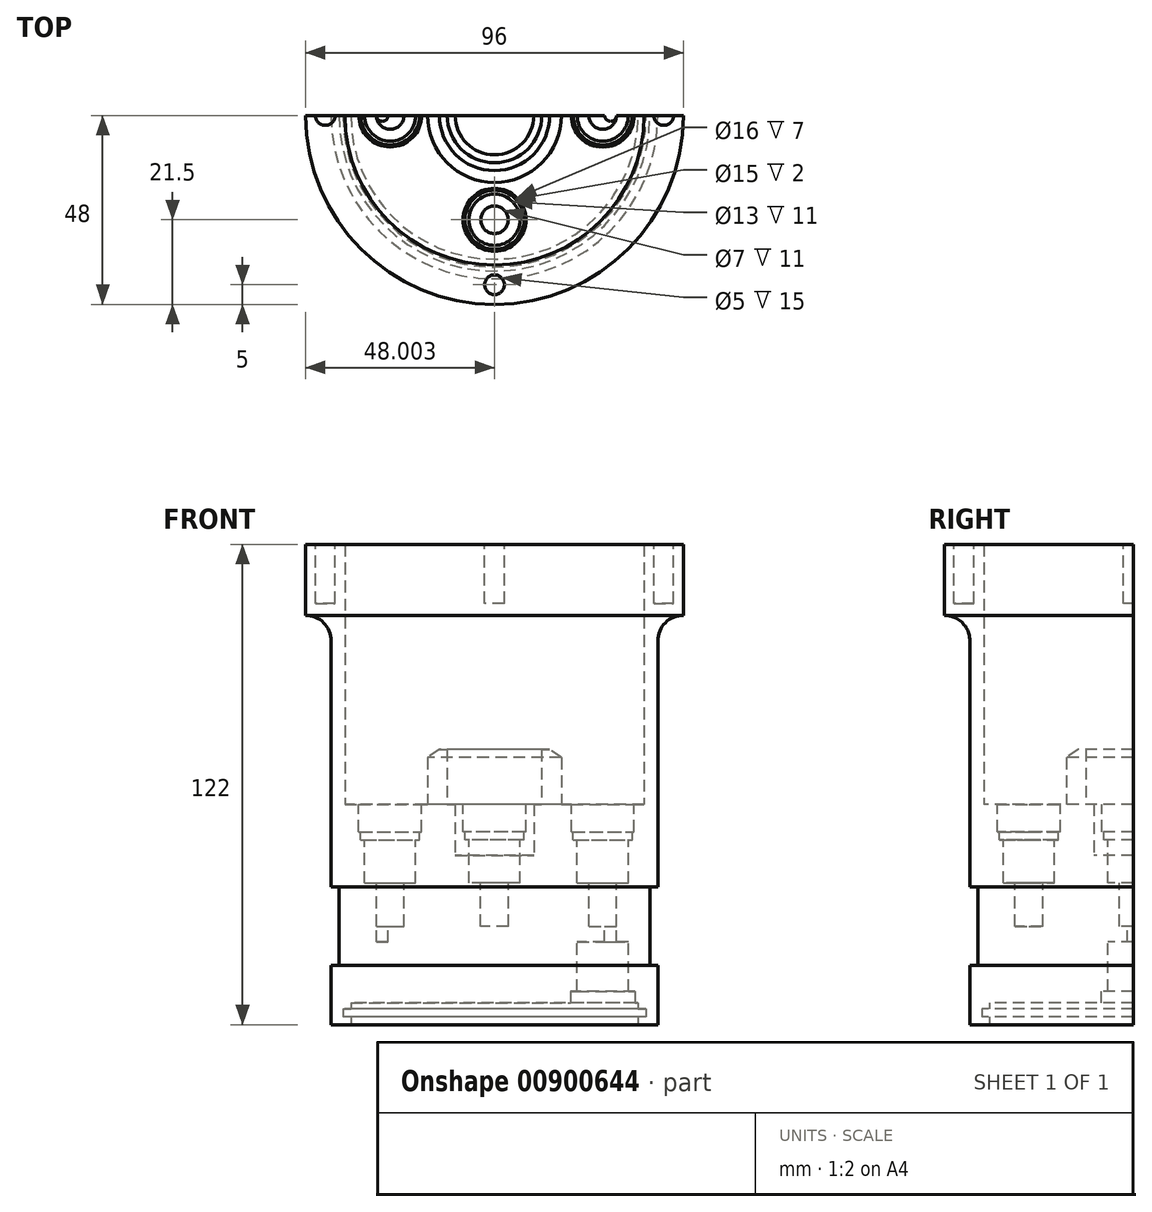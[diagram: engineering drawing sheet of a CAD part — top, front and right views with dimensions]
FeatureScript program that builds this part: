
annotation { "Feature Type Name" : "Feature", "Feature Type Description" : "" }
export const myFeature = defineFeature(function(context is Context, id is Id, definition is map)
    precondition{}
    {
        {
            var Q0;
            Q0=qCreatedBy(makeId("Front.planeOp"),FACE);
            var sketch = newSketch(context, id + "F0", { "sketchPlane" : qUnion([Q0])});
            skLineSegment(sketch, "E0.bottom", {"start": v(54.77, 57.03) * mm, "end": v(58.27, 57.03) * mm});
            skLineSegment(sketch, "E0.top", {"start": v(53.27, -64.97) * mm, "end": v(58.27, -64.97) * mm});
            skLineSegment(sketch, "E0.right", {"start": v(58.27, 32.53) * mm, "end": v(58.27, -29.97) * mm});
            skLineSegment(sketch, "E1", {"start": v(54.77, 57.03) * mm, "end": v(54.77, -8.97) * mm});
            skLineSegment(sketch, "E2", {"start": v(54.77, -8.97) * mm, "end": v(33.77, -8.97) * mm});
            skLineSegment(sketch, "E3.top", {"start": v(30.77, 4.9) * mm, "end": v(28.77, 4.9) * mm});
            skLineSegment(sketch, "E3.left", {"start": v(33.77, -8.97) * mm, "end": v(33.77, 2.9) * mm});
            skLineSegment(sketch, "E3.right", {"start": v(28.77, -8.97) * mm, "end": v(28.77, 4.9) * mm});
            skLineSegment(sketch, "E4", {"start": v(30.77, 4.9) * mm, "end": v(33.77, 2.9) * mm});
            skPoint(sketch, "E5.orphan", {"position": v(33.77, 4.9) * mm});
            skLineSegment(sketch, "E6.trimOffspring", {"start": v(28.77, -8.97) * mm, "end": v(26.77, -8.97) * mm});
            skLineSegment(sketch, "E7.left", {"start": v(26.77, -8.97) * mm, "end": v(26.77, -10.97) * mm});
            skLineSegment(sketch, "E8.top", {"start": v(26.77, -21.97) * mm, "end": v(16.77, -21.97) * mm});
            skLineSegment(sketch, "E8.left", {"start": v(26.77, -10.97) * mm, "end": v(26.77, -21.97) * mm});
            skLineSegment(sketch, "E9.trimOffspring", {"start": v(16.77, -21.97) * mm, "end": v(16.77, -59.47) * mm});
            skLineSegment(sketch, "E10", {"start": v(58.27, -29.97) * mm, "end": v(56.27, -29.97) * mm});
            skLineSegment(sketch, "E11", {"start": v(56.27, -29.97) * mm, "end": v(56.27, -49.97) * mm});
            skLineSegment(sketch, "E12", {"start": v(56.27, -49.97) * mm, "end": v(58.27, -49.97) * mm});
            skLineSegment(sketch, "E13.trimOffspring", {"start": v(58.27, -49.97) * mm, "end": v(58.27, -64.97) * mm});
            skLineSegment(sketch, "E14", {"start": v(53.27, -64.97) * mm, "end": v(53.27, -62.97) * mm});
            skLineSegment(sketch, "E15", {"start": v(55.27, -62.97) * mm, "end": v(55.27, -60.97) * mm});
            skLineSegment(sketch, "E16", {"start": v(55.27, -60.97) * mm, "end": v(53.27, -60.97) * mm});
            skLineSegment(sketch, "E17", {"start": v(53.27, -62.97) * mm, "end": v(55.27, -62.97) * mm});
            skLineSegment(sketch, "E18", {"start": v(53.27, -60.97) * mm, "end": v(53.27, -59.47) * mm});
            skLineSegment(sketch, "E19", {"start": v(53.27, -59.47) * mm, "end": v(16.77, -59.47) * mm});
            skLineSegment(sketch, "E20", {"start": v(16.77, -29.96) * mm, "end": v(16.77, 7.54) * mm, "construction": true});
            skLineSegment(sketch, "E21.bottom", {"start": v(58.27, 57.03) * mm, "end": v(64.77, 57.03) * mm});
            skLineSegment(sketch, "E21.right", {"start": v(64.77, 57.03) * mm, "end": v(64.77, 39.03) * mm});
            skLineSegment(sketch, "E22.top", {"start": v(58.27, 32.53) * mm, "end": v(64.77, 32.53) * mm, "construction": true});
            skLineSegment(sketch, "E22.right", {"start": v(64.77, 39.03) * mm, "end": v(64.77, 32.53) * mm, "construction": true});
            skArc(sketch, "E23", {"start": v(64.77, 39.03) * mm, "mid": v(60.18, 37.13) * mm, "end": v(58.27, 32.53) * mm});
            skSolve(sketch);
        }
        {
            var Q0;
            Q0=makeQuery(id+"F0.imprint","IMPRINT",FACE,{"disambiguationData":[TD([[makeQuery(id+"F0.imprint","IMPRINT",EDGE,{"derivedFrom":sQuery(id+"F0.wireOp",EDGE,"E0.bottom")}),-1.0]])]});
            var Q1;
            Q1=sQuery(id+"F0.wireOp",EDGE,"E20");
            revolve(context, id + "F1", {"surfaceOperationType" : NewSurfaceOperationType.NEW, "entities" : qUnion([Q0]), "axis" : qUnion([Q1]), "revolveType" : RevolveType.FULL});
        }
        {
            var Q0;
            Q0=qCreatedBy(makeId("Front.planeOp"),FACE);
            var sketch = newSketch(context, id + "F2", { "sketchPlane" : qUnion([Q0])});
            skLineSegment(sketch, "E24.bottom", {"start": v(-36.49, 60.26) * mm, "end": v(67.45, 60.26) * mm});
            skLineSegment(sketch, "E24.top", {"start": v(-36.49, -71.1) * mm, "end": v(67.45, -71.1) * mm});
            skLineSegment(sketch, "E24.left", {"start": v(-36.49, 60.26) * mm, "end": v(-36.49, -71.1) * mm});
            skLineSegment(sketch, "E24.right", {"start": v(67.45, 60.26) * mm, "end": v(67.45, -71.1) * mm});
            skSolve(sketch);
        }
        {
            var Q0;
            Q0=makeQuery(id+"F2.imprint","IMPRINT",FACE,{"disambiguationData":[TD([[makeQuery(id+"F2.imprint","IMPRINT",EDGE,{"derivedFrom":sQuery(id+"F2.wireOp",EDGE,"E24.bottom")}),-1.0]])]});
            extrude(context, id + "F3", {"entities" : qUnion([Q0]), "operationType" : NewBodyOperationType.REMOVE, "oppositeDirection" : true, "depth" : 50 * mm, "offsetDistance" : 25 * mm});
        }
        {
            var Q0;
            Q0=makeQuery(id+"F1.opRevolve","SWEPT_FACE",FACE,{"disambiguationData":[OSD([sQuery(id+"F0.wireOp",EDGE,"E2")])]});
            var sketch = newSketch(context, id + "F4", { "sketchPlane" : qUnion([Q0])});
            skArc(sketch, "E25", {"start": v(-17.73, 0) * mm, "mid": v(-9.73, -8) * mm, "end": v(-1.73, 0) * mm});
            skLineSegment(sketch, "E26", {"start": v(-17.73, 0) * mm, "end": v(-1.73, 0) * mm});
            skArc(sketch, "E27", {"start": v(36.27, 0) * mm, "mid": v(44.27, -8) * mm, "end": v(52.27, 0) * mm});
            skLineSegment(sketch, "E28", {"start": v(36.27, 0) * mm, "end": v(52.27, 0) * mm});
            skCircle(sketch, "E29", {"center": v(16.77, -26.5) * mm, "radius": 8 * mm});
            skPoint(sketch, "E29.centerSnap0", {"position": v(16.77, -17) * mm});
            skSolve(sketch);
        }
        {
            var Q0;
            Q0=makeQuery(id+"F4.imprint","IMPRINT",FACE,{"disambiguationData":[TD([[makeQuery(id+"F4.imprint","IMPRINT",EDGE,{"derivedFrom":sQuery(id+"F4.wireOp",EDGE,"E25")}),1.0]])]});
            var Q1;
            Q1=makeQuery(id+"F4.imprint","IMPRINT",FACE,{"disambiguationData":[TD([[makeQuery(id+"F4.imprint","IMPRINT",EDGE,{"derivedFrom":sQuery(id+"F4.wireOp",EDGE,"E27")}),1.0]])]});
            var Q2;
            Q2=makeQuery(id+"F4.imprint","IMPRINT",FACE,{"disambiguationData":[TD([[makeQuery(id+"F4.imprint","IMPRINT",EDGE,{"derivedFrom":sQuery(id+"F4.wireOp",EDGE,"E29")}),1.0]])]});
            extrude(context, id + "F5", {"entities" : qUnion([Q0, Q1, Q2]), "operationType" : NewBodyOperationType.REMOVE, "oppositeDirection" : true, "depth" : 7 * mm, "offsetDistance" : 25 * mm});
        }
        {
            var Q0;
            Q0=makeQuery(id+"F5.boolean.opBoolean","COPY",FACE,{"derivedFrom":makeQuery(id+"F5.opExtrude","CAP_FACE",FACE,{"disambiguationData":[OSD([sQuery(id+"F4.wireOp",EDGE,"E25"),sQuery(id+"F4.wireOp",EDGE,"E26")])],"isStart":false})});
            var sketch = newSketch(context, id + "F6", { "sketchPlane" : qUnion([Q0])});
            skArc(sketch, "E30", {"start": v(-17.23, 0) * mm, "mid": v(-9.73, -7.5) * mm, "end": v(-2.23, 0) * mm});
            skLineSegment(sketch, "E31", {"start": v(-17.23, 0) * mm, "end": v(-2.23, 0) * mm});
            skArc(sketch, "E32", {"start": v(36.77, 0) * mm, "mid": v(44.27, -7.5) * mm, "end": v(51.77, 0) * mm});
            skLineSegment(sketch, "E33", {"start": v(36.77, 0) * mm, "end": v(51.77, 0) * mm});
            skCircle(sketch, "E34", {"center": v(16.77, -26.5) * mm, "radius": 7.5 * mm});
            skSolve(sketch);
        }
        {
            var Q0;
            Q0=makeQuery(id+"F6.imprint","IMPRINT",FACE,{"disambiguationData":[TD([[makeQuery(id+"F6.imprint","IMPRINT",EDGE,{"derivedFrom":sQuery(id+"F6.wireOp",EDGE,"E30")}),1.0]])]});
            var Q1;
            Q1=makeQuery(id+"F6.imprint","IMPRINT",FACE,{"disambiguationData":[TD([[makeQuery(id+"F6.imprint","IMPRINT",EDGE,{"derivedFrom":sQuery(id+"F6.wireOp",EDGE,"E32")}),1.0]])]});
            var Q2;
            Q2=makeQuery(id+"F6.imprint","IMPRINT",FACE,{"disambiguationData":[TD([[makeQuery(id+"F6.imprint","IMPRINT",EDGE,{"derivedFrom":sQuery(id+"F6.wireOp",EDGE,"E34")}),1.0]])]});
            extrude(context, id + "F7", {"entities" : qUnion([Q0, Q1, Q2]), "operationType" : NewBodyOperationType.REMOVE, "oppositeDirection" : true, "depth" : 2 * mm, "offsetDistance" : 25 * mm});
        }
        {
            var Q0;
            Q0=makeQuery(id+"F7.boolean.opBoolean","COPY",FACE,{"derivedFrom":makeQuery(id+"F7.opExtrude","CAP_FACE",FACE,{"disambiguationData":[OSD([sQuery(id+"F6.wireOp",EDGE,"E30"),sQuery(id+"F6.wireOp",EDGE,"E31")])],"isStart":false})});
            var sketch = newSketch(context, id + "F8", { "sketchPlane" : qUnion([Q0])});
            skArc(sketch, "E35", {"start": v(-16.23, 0) * mm, "mid": v(-9.73, -6.5) * mm, "end": v(-3.23, 0) * mm});
            skLineSegment(sketch, "E36", {"start": v(-16.23, 0) * mm, "end": v(-3.23, 0) * mm});
            skArc(sketch, "E37", {"start": v(37.77, 0) * mm, "mid": v(44.27, -6.5) * mm, "end": v(50.77, 0) * mm});
            skLineSegment(sketch, "E38", {"start": v(37.77, 0) * mm, "end": v(50.77, 0) * mm});
            skCircle(sketch, "E39", {"center": v(16.77, -26.5) * mm, "radius": 6.5 * mm});
            skSolve(sketch);
        }
        {
            var Q0;
            Q0=makeQuery(id+"F8.imprint","IMPRINT",FACE,{"disambiguationData":[TD([[makeQuery(id+"F8.imprint","IMPRINT",EDGE,{"derivedFrom":sQuery(id+"F8.wireOp",EDGE,"E35")}),1.0]])]});
            var Q1;
            Q1=makeQuery(id+"F8.imprint","IMPRINT",FACE,{"disambiguationData":[TD([[makeQuery(id+"F8.imprint","IMPRINT",EDGE,{"derivedFrom":sQuery(id+"F8.wireOp",EDGE,"E37")}),1.0]])]});
            var Q2;
            Q2=makeQuery(id+"F8.imprint","IMPRINT",FACE,{"disambiguationData":[TD([[makeQuery(id+"F8.imprint","IMPRINT",EDGE,{"derivedFrom":sQuery(id+"F8.wireOp",EDGE,"E39")}),1.0]])]});
            extrude(context, id + "F9", {"entities" : qUnion([Q0, Q1, Q2]), "operationType" : NewBodyOperationType.REMOVE, "oppositeDirection" : true, "depth" : 11 * mm, "offsetDistance" : 25 * mm});
        }
        {
            var Q0;
            Q0=makeQuery(id+"F9.boolean.opBoolean","COPY",FACE,{"derivedFrom":makeQuery(id+"F9.opExtrude","CAP_FACE",FACE,{"disambiguationData":[OSD([sQuery(id+"F8.wireOp",EDGE,"E35"),sQuery(id+"F8.wireOp",EDGE,"E36")])],"isStart":false})});
            var sketch = newSketch(context, id + "F10", { "sketchPlane" : qUnion([Q0])});
            skArc(sketch, "E40", {"start": v(-13.23, 0) * mm, "mid": v(-9.73, -3.5) * mm, "end": v(-6.23, 0) * mm});
            skLineSegment(sketch, "E41", {"start": v(-13.23, 0) * mm, "end": v(-6.23, 0) * mm});
            skArc(sketch, "E42", {"start": v(40.77, 0) * mm, "mid": v(44.27, -3.5) * mm, "end": v(47.77, 0) * mm});
            skLineSegment(sketch, "E43", {"start": v(40.77, 0) * mm, "end": v(47.77, 0) * mm});
            skCircle(sketch, "E44", {"center": v(16.77, -26.5) * mm, "radius": 3.5 * mm});
            skSolve(sketch);
        }
        {
            var Q0;
            Q0=makeQuery(id+"F10.imprint","IMPRINT",FACE,{"disambiguationData":[TD([[makeQuery(id+"F10.imprint","IMPRINT",EDGE,{"derivedFrom":sQuery(id+"F10.wireOp",EDGE,"E40")}),1.0]])]});
            var Q1;
            Q1=makeQuery(id+"F10.imprint","IMPRINT",FACE,{"disambiguationData":[TD([[makeQuery(id+"F10.imprint","IMPRINT",EDGE,{"derivedFrom":sQuery(id+"F10.wireOp",EDGE,"E42")}),1.0]])]});
            var Q2;
            Q2=makeQuery(id+"F10.imprint","IMPRINT",FACE,{"disambiguationData":[TD([[makeQuery(id+"F10.imprint","IMPRINT",EDGE,{"derivedFrom":sQuery(id+"F10.wireOp",EDGE,"E44")}),1.0]])]});
            extrude(context, id + "F11", {"entities" : qUnion([Q0, Q1, Q2]), "operationType" : NewBodyOperationType.REMOVE, "oppositeDirection" : true, "depth" : 11 * mm, "offsetDistance" : 25 * mm});
        }
        {
            var Q0;
            Q0=makeQuery(id+"F11.boolean.opBoolean","COPY",FACE,{"derivedFrom":makeQuery(id+"F11.opExtrude","CAP_FACE",FACE,{"disambiguationData":[OSD([sQuery(id+"F10.wireOp",EDGE,"E42"),sQuery(id+"F10.wireOp",EDGE,"E43")])],"isStart":false})});
            var sketch = newSketch(context, id + "F12", { "sketchPlane" : qUnion([Q0])});
            skCircle(sketch, "E45", {"center": v(46.27, 0) * mm, "radius": 1.5 * mm});
            skCircle(sketch, "E46", {"center": v(-11.73, 0) * mm, "radius": 1.5 * mm});
            skSolve(sketch);
        }
        {
            var Q0;
            Q0=makeQuery(id+"F12.imprint","IMPRINT",FACE,{"disambiguationData":[TD([[makeQuery(id+"F12.imprint","IMPRINT",EDGE,{"derivedFrom":sQuery(id+"F12.wireOp",EDGE,"E46")}),1.0]])]});
            var Q1;
            {var subQ0=sQuery(id+"F12.wireOp",EDGE,"E45");var subQ1=makeQuery(id+"F11.boolean.opBoolean","COPY",EDGE,{"derivedFrom":makeQuery(id+"F11.opExtrude","CAP_EDGE",EDGE,{"disambiguationData":[OSD([sQuery(id+"F10.wireOp",EDGE,"E43")])],"isStart":false})});var subQ3=makeQuery(id+"F12.imprint","INTERSECT",VERTEX,{"derivedFrom":[subQ1,subQ0]});Q1=makeQuery(id+"F12.imprint","IMPRINT",FACE,{"disambiguationData":[TD([[makeQuery(id+"F12.imprint","IMPRINT",EDGE,{"disambiguationData":[TD([[subQ3,-1.0]])],"derivedFrom":subQ0}),1.0]])]});}
            extrude(context, id + "F13", {"entities" : qUnion([Q0, Q1]), "operationType" : NewBodyOperationType.REMOVE, "oppositeDirection" : true, "depth" : 4 * mm, "offsetDistance" : 25 * mm});
        }
        {
            var Q0;
            Q0=makeQuery(id+"F1.opRevolve","SWEPT_FACE",FACE,{"disambiguationData":[OSD([sQuery(id+"F0.wireOp",EDGE,"E0.bottom"),sQuery(id+"F0.wireOp",EDGE,"E21.bottom")])]});
            var sketch = newSketch(context, id + "F14", { "sketchPlane" : qUnion([Q0])});
            skCircle(sketch, "E47", {"center": v(59.77, 0) * mm, "radius": 2.5 * mm});
            skCircle(sketch, "E48", {"center": v(16.77, -43) * mm, "radius": 2.5 * mm});
            skPoint(sketch, "E48.centerSnap0", {"position": v(16.77, -48) * mm});
            skCircle(sketch, "E49", {"center": v(-26.23, 0) * mm, "radius": 2.5 * mm});
            skSolve(sketch);
        }
        {
            var Q0;
            {var subQ0=sQuery(id+"F14.wireOp",EDGE,"E49");var subQ1=makeQuery(id+"F3.boolean.opBoolean","INTERSECT",EDGE,{"disambiguationData":[OD(0.0)],"derivedFrom":[makeQuery(id+"F1.opRevolve","SWEPT_FACE",FACE,{"disambiguationData":[OSD([sQuery(id+"F0.wireOp",EDGE,"E0.bottom"),sQuery(id+"F0.wireOp",EDGE,"E21.bottom")])]}),makeQuery(id+"F3.opExtrude","CAP_FACE",FACE,{"disambiguationData":[OSD([sQuery(id+"F2.wireOp",EDGE,"E24.bottom"),sQuery(id+"F2.wireOp",EDGE,"E24.top"),sQuery(id+"F2.wireOp",EDGE,"E24.left"),sQuery(id+"F2.wireOp",EDGE,"E24.right")])],"isStart":true})]});var subQ2=makeQuery(id+"F14.imprint","INTERSECT",VERTEX,{"disambiguationData":[OD(0.0)],"derivedFrom":[subQ1,subQ0]});Q0=makeQuery(id+"F14.imprint","IMPRINT",FACE,{"disambiguationData":[TD([[makeQuery(id+"F14.imprint","IMPRINT",EDGE,{"disambiguationData":[TD([[subQ2,1.0]])],"derivedFrom":subQ0}),1.0]])]});}
            var Q1;
            Q1=makeQuery(id+"F14.imprint","IMPRINT",FACE,{"disambiguationData":[TD([[makeQuery(id+"F14.imprint","IMPRINT",EDGE,{"derivedFrom":sQuery(id+"F14.wireOp",EDGE,"E48")}),1.0]])]});
            var Q2;
            {var subQ0=sQuery(id+"F14.wireOp",EDGE,"E47");var subQ1=makeQuery(id+"F3.boolean.opBoolean","INTERSECT",EDGE,{"disambiguationData":[OD(1.0)],"derivedFrom":[makeQuery(id+"F1.opRevolve","SWEPT_FACE",FACE,{"disambiguationData":[OSD([sQuery(id+"F0.wireOp",EDGE,"E0.bottom"),sQuery(id+"F0.wireOp",EDGE,"E21.bottom")])]}),makeQuery(id+"F3.opExtrude","CAP_FACE",FACE,{"disambiguationData":[OSD([sQuery(id+"F2.wireOp",EDGE,"E24.bottom"),sQuery(id+"F2.wireOp",EDGE,"E24.top"),sQuery(id+"F2.wireOp",EDGE,"E24.left"),sQuery(id+"F2.wireOp",EDGE,"E24.right")])],"isStart":true})]});var subQ2=makeQuery(id+"F14.imprint","INTERSECT",VERTEX,{"disambiguationData":[OD(0.0)],"derivedFrom":[subQ1,subQ0]});Q2=makeQuery(id+"F14.imprint","IMPRINT",FACE,{"disambiguationData":[TD([[makeQuery(id+"F14.imprint","IMPRINT",EDGE,{"disambiguationData":[TD([[subQ2,-1.0]])],"derivedFrom":subQ0}),1.0]])]});}
            extrude(context, id + "F15", {"entities" : qUnion([Q0, Q1, Q2]), "operationType" : NewBodyOperationType.REMOVE, "oppositeDirection" : true, "depth" : 15 * mm, "offsetDistance" : 25 * mm});
        }
        {
            var Q0;
            Q0=makeQuery(id+"F11.boolean.opBoolean","COPY",FACE,{"derivedFrom":makeQuery(id+"F11.opExtrude","CAP_FACE",FACE,{"disambiguationData":[OSD([sQuery(id+"F10.wireOp",EDGE,"E42"),sQuery(id+"F10.wireOp",EDGE,"E43")])],"isStart":false})});
            var sketch = newSketch(context, id + "F16", { "sketchPlane" : qUnion([Q0])});
            skCircle(sketch, "E50", {"center": v(44.27, 0) * mm, "radius": 6.5 * mm});
            skSolve(sketch);
        }
        {
            var Q0;
            Q0=makeQuery(id+"F16.imprint","IMPRINT",FACE,{"disambiguationData":[TD([[makeQuery(id+"F16.imprint","IMPRINT",EDGE,{"derivedFrom":sQuery(id+"F16.wireOp",EDGE,"E50")}),1.0]])]});
            var Q1;
            Q1=makeQuery(id+"F16.imprint","IMPRINT",FACE,{"disambiguationData":[TD([[makeQuery(id+"F16.imprint","IMPRINT",EDGE,{"derivedFrom":makeQuery(id+"F11.boolean.opBoolean","COPY",EDGE,{"derivedFrom":makeQuery(id+"F11.opExtrude","CAP_EDGE",EDGE,{"disambiguationData":[OSD([sQuery(id+"F10.wireOp",EDGE,"E42")])],"isStart":false})})}),1.0]])]});
            extrude(context, id + "F17", {"entities" : qUnion([Q0, Q1]), "operationType" : NewBodyOperationType.REMOVE, "endBound" : BoundingType.THROUGH_ALL, "oppositeDirection" : true, "depth" : 25 * mm, "offsetDistance" : 25 * mm, "hasSecondDirection" : true, "secondDirectionOppositeDirection" : true, "secondDirectionDepth" : 4 * mm});
        }
        {
            var Q0;
            Q0=makeQuery(id+"F1.opRevolve","SWEPT_FACE",FACE,{"disambiguationData":[OSD([sQuery(id+"F0.wireOp",EDGE,"E19")])]});
            var sketch = newSketch(context, id + "F18", { "sketchPlane" : qUnion([Q0])});
            skCircle(sketch, "E51", {"center": v(44.27, 0) * mm, "radius": 8.25 * mm});
            skSolve(sketch);
        }
        {
            var Q0;
            {var subQ1=makeQuery(id+"F1.opRevolve","SWEPT_FACE",FACE,{"disambiguationData":[OSD([sQuery(id+"F0.wireOp",EDGE,"E19")])]});var subQ7=makeQuery(id+"F17.boolean.opBoolean","INTERSECT",EDGE,{"derivedFrom":[subQ1,makeQuery(id+"F17.opExtrude","SWEPT_FACE",FACE,{"disambiguationData":[OSD([sQuery(id+"F16.wireOp",EDGE,"E50")])]})]});Q0=makeQuery(id+"F18.imprint","IMPRINT",FACE,{"disambiguationData":[TD([[makeQuery(id+"F18.imprint","IMPRINT",EDGE,{"derivedFrom":subQ7}),1.0]])]});}
            extrude(context, id + "F19", {"entities" : qUnion([Q0]), "operationType" : NewBodyOperationType.REMOVE, "oppositeDirection" : true, "depth" : 3 * mm, "offsetDistance" : 25 * mm});
        }
    });
